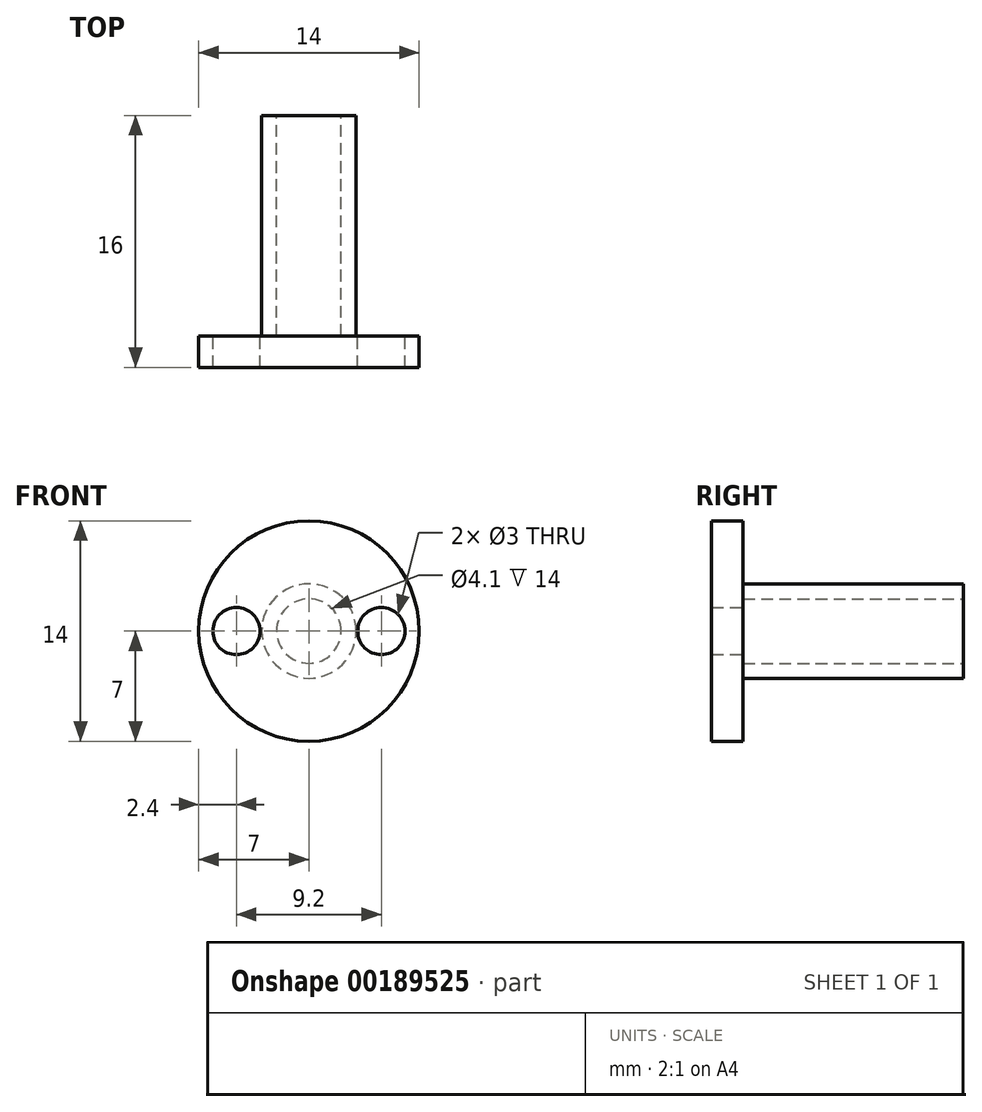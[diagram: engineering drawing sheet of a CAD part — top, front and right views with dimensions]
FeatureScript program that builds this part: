
annotation { "Feature Type Name" : "Feature", "Feature Type Description" : "" }
export const myFeature = defineFeature(function(context is Context, id is Id, definition is map)
    precondition{}
    {
        {
            var Q0;
            Q0=qCreatedBy(makeId("Front.planeOp"),FACE);
            var sketch = newSketch(context, id + "F0", { "sketchPlane" : qUnion([Q0])});
            skCircle(sketch, "E0", {"center": v(0, 0) * mm, "radius": 7 * mm});
            skCircle(sketch, "E1", {"center": v(-4.6, 0) * mm, "radius": 1.5 * mm});
            skCircle(sketch, "E2.MirrorC", {"center": v(4.6, 0) * mm, "radius": 1.5 * mm});
            skCircle(sketch, "E3", {"center": v(0, 0) * mm, "radius": 3 * mm});
            skSolve(sketch);
        }
        {
            var Q0;
            Q0=makeQuery(id+"F0.imprint","IMPRINT",FACE,{"disambiguationData":[TD([[makeQuery(id+"F0.imprint","IMPRINT",EDGE,{"derivedFrom":sQuery(id+"F0.wireOp",EDGE,"E0")}),1.0]])]});
            var Q1;
            {var subQ0=sQuery(id+"F0.wireOp",EDGE,"E3");var subQ1=sQuery(id+"F0.wireOp",EDGE,"E1");var subQ2=makeQuery(id+"F0.imprint","INTERSECT",VERTEX,{"disambiguationData":[OD(0.0)],"derivedFrom":[subQ1,subQ0]});Q1=makeQuery(id+"F0.imprint","IMPRINT",FACE,{"disambiguationData":[TD([[makeQuery(id+"F0.imprint","IMPRINT",EDGE,{"disambiguationData":[TD([[subQ2,1.0]])],"derivedFrom":subQ1}),-1.0]])]});}
            var Q2;
            Q2=makeQuery(id+"F0.imprint","IMPRINT",FACE,{"disambiguationData":[TD([[makeQuery(id+"F0.imprint","IMPRINT",EDGE,{"derivedFrom":sQuery(id+"F0.wireOp",EDGE,"E3")}),1.0]])]});
            extrude(context, id + "F1", {"entities" : qUnion([Q0, Q1, Q2]), "depth" : 2 * mm});
        }
        {
            var Q0;
            Q0=makeQuery(id+"F0.imprint","IMPRINT",FACE,{"disambiguationData":[TD([[makeQuery(id+"F0.imprint","IMPRINT",EDGE,{"derivedFrom":sQuery(id+"F0.wireOp",EDGE,"E3")}),1.0]])]});
            extrude(context, id + "F2", {"entities" : qUnion([Q0]), "operationType" : NewBodyOperationType.ADD, "oppositeDirection" : true, "depth" : 14 * mm});
        }
        {
            var Q0;
            Q0=makeQuery(id+"F2.opExtrude","CAP_FACE",FACE,{"disambiguationData":[OSD([sQuery(id+"F0.wireOp",EDGE,"E3")])],"isStart":false});
            var sketch = newSketch(context, id + "F3", { "sketchPlane" : qUnion([Q0])});
            skCircle(sketch, "E4", {"center": v(0, 0) * mm, "radius": 2.05 * mm});
            skSolve(sketch);
        }
        {
            var Q0;
            Q0=makeQuery(id+"F3.imprint","IMPRINT",FACE,{"disambiguationData":[TD([[makeQuery(id+"F3.imprint","IMPRINT",EDGE,{"derivedFrom":sQuery(id+"F3.wireOp",EDGE,"E4")}),1.0]])]});
            extrude(context, id + "F4", {"entities" : qUnion([Q0]), "operationType" : NewBodyOperationType.REMOVE, "oppositeDirection" : true, "depth" : 14 * mm});
        }
    });
